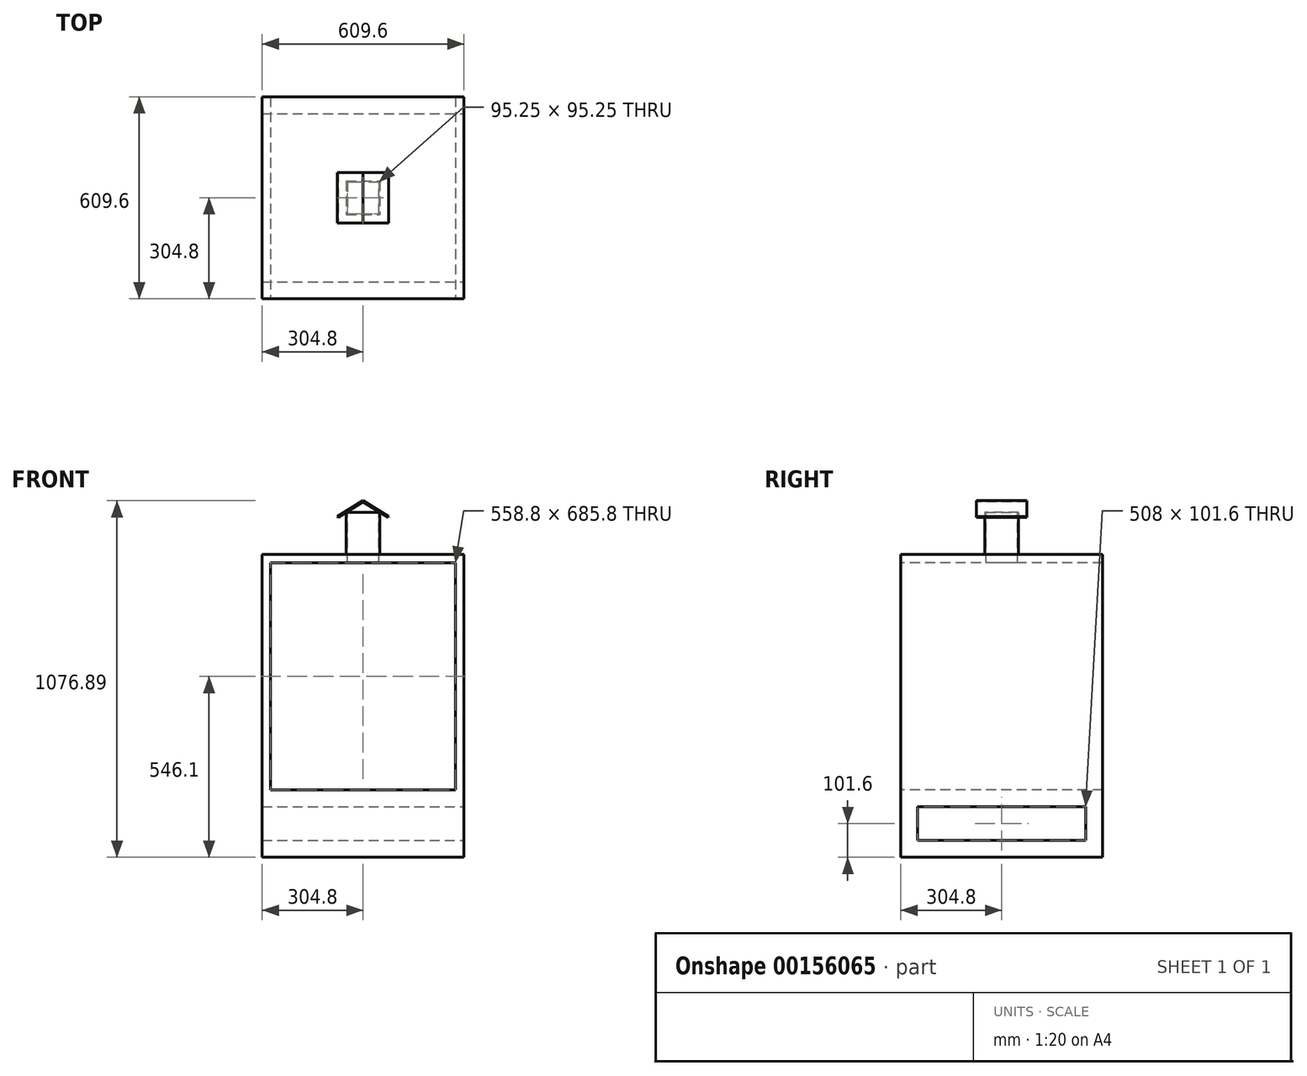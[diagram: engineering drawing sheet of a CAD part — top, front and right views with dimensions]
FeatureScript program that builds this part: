
annotation { "Feature Type Name" : "Feature", "Feature Type Description" : "" }
export const myFeature = defineFeature(function(context is Context, id is Id, definition is map)
    precondition{}
    {
        {
            var Q0;
            Q0=qCreatedBy(makeId("Top.planeOp"),FACE);
            var sketch = newSketch(context, id + "F0", { "sketchPlane" : qUnion([Q0])});
            skLineSegment(sketch, "E0.bottom", {"start": v(0, 0) * mm, "end": v(609.6, 0) * mm});
            skLineSegment(sketch, "E0.top", {"start": v(0, -609.6) * mm, "end": v(609.6, -609.6) * mm});
            skLineSegment(sketch, "E0.left", {"start": v(0, 0) * mm, "end": v(0, -609.6) * mm});
            skLineSegment(sketch, "E0.right", {"start": v(609.6, 0) * mm, "end": v(609.6, -609.6) * mm});
            skSolve(sketch);
        }
        {
            var Q0;
            Q0 = qSketchRegion(id + "F0", true);
            extrude(context, id + "F1", {"entities" : qUnion([Q0]), "depth" : 914.4 * mm});
        }
        {
            var Q0;
            Q0=makeQuery(id+"F1.opExtrude","SWEPT_FACE",FACE,{"disambiguationData":[OSD([sQuery(id+"F0.wireOp",EDGE,"E0.top")])]});
            var sketch = newSketch(context, id + "F2", { "sketchPlane" : qUnion([Q0])});
            skLineSegment(sketch, "E1.bottom", {"start": v(25.4, 889) * mm, "end": v(584.2, 889) * mm});
            skLineSegment(sketch, "E1.top", {"start": v(25.4, 203.2) * mm, "end": v(584.2, 203.2) * mm});
            skLineSegment(sketch, "E1.left", {"start": v(25.4, 889) * mm, "end": v(25.4, 203.2) * mm});
            skLineSegment(sketch, "E1.right", {"start": v(584.2, 889) * mm, "end": v(584.2, 203.2) * mm});
            skSolve(sketch);
        }
        {
            var Q0;
            Q0=makeQuery(id+"F2.imprint","IMPRINT",FACE,{"disambiguationData":[TD([[makeQuery(id+"F2.imprint","IMPRINT",EDGE,{"derivedFrom":sQuery(id+"F2.wireOp",EDGE,"E1.bottom")}),-1.0]])]});
            extrude(context, id + "F3", {"entities" : qUnion([Q0]), "operationType" : NewBodyOperationType.REMOVE, "endBound" : BoundingType.UP_TO_NEXT, "oppositeDirection" : true, "depth" : 25.4 * mm});
        }
        {
            var Q0;
            Q0=makeQuery(id+"F1.opExtrude","SWEPT_FACE",FACE,{"disambiguationData":[OSD([sQuery(id+"F0.wireOp",EDGE,"E0.right")])]});
            var sketch = newSketch(context, id + "F4", { "sketchPlane" : qUnion([Q0])});
            skLineSegment(sketch, "E2.bottom", {"start": v(-558.8, 50.8) * mm, "end": v(-50.8, 50.8) * mm});
            skLineSegment(sketch, "E2.top", {"start": v(-558.8, 152.4) * mm, "end": v(-50.8, 152.4) * mm});
            skLineSegment(sketch, "E2.left", {"start": v(-558.8, 50.8) * mm, "end": v(-558.8, 152.4) * mm});
            skLineSegment(sketch, "E2.right", {"start": v(-50.8, 50.8) * mm, "end": v(-50.8, 152.4) * mm});
            skSolve(sketch);
        }
        {
            var Q0;
            Q0=makeQuery(id+"F4.imprint","IMPRINT",FACE,{"disambiguationData":[TD([[makeQuery(id+"F4.imprint","IMPRINT",EDGE,{"derivedFrom":sQuery(id+"F4.wireOp",EDGE,"E2.bottom")}),1.0]])]});
            extrude(context, id + "F5", {"entities" : qUnion([Q0]), "operationType" : NewBodyOperationType.REMOVE, "endBound" : BoundingType.UP_TO_NEXT, "oppositeDirection" : true, "depth" : 25.4 * mm});
        }
        {
            var Q0;
            Q0=makeQuery(id+"F1.opExtrude","CAP_FACE",FACE,{"disambiguationData":[OSD([sQuery(id+"F0.wireOp",EDGE,"E0.bottom"),sQuery(id+"F0.wireOp",EDGE,"E0.top"),sQuery(id+"F0.wireOp",EDGE,"E0.left"),sQuery(id+"F0.wireOp",EDGE,"E0.right")])],"isStart":false});
            var sketch = newSketch(context, id + "F6", { "sketchPlane" : qUnion([Q0])});
            skLineSegment(sketch, "E3.bottom", {"start": v(254, -254) * mm, "end": v(355.6, -254) * mm});
            skLineSegment(sketch, "E3.top", {"start": v(254, -355.6) * mm, "end": v(355.6, -355.6) * mm});
            skLineSegment(sketch, "E3.left", {"start": v(254, -254) * mm, "end": v(254, -355.6) * mm});
            skLineSegment(sketch, "E3.right", {"start": v(355.6, -254) * mm, "end": v(355.6, -355.6) * mm});
            skSolve(sketch);
        }
        {
            var Q0;
            Q0=makeQuery(id+"F6.imprint","IMPRINT",FACE,{"disambiguationData":[TD([[makeQuery(id+"F6.imprint","IMPRINT",EDGE,{"derivedFrom":sQuery(id+"F6.wireOp",EDGE,"E3.bottom")}),-1.0]])]});
            extrude(context, id + "F7", {"entities" : qUnion([Q0]), "operationType" : NewBodyOperationType.ADD, "depth" : 127 * mm});
        }
        {
            var Q0;
            Q0=makeQuery(id+"F7.opExtrude","CAP_FACE",FACE,{"disambiguationData":[OSD([sQuery(id+"F6.wireOp",EDGE,"E3.bottom"),sQuery(id+"F6.wireOp",EDGE,"E3.top"),sQuery(id+"F6.wireOp",EDGE,"E3.left"),sQuery(id+"F6.wireOp",EDGE,"E3.right")])],"isStart":false});
            var sketch = newSketch(context, id + "F8", { "sketchPlane" : qUnion([Q0])});
            skLineSegment(sketch, "E4.0", {"start": v(352.42, -257.17) * mm, "end": v(257.17, -257.17) * mm});
            skLineSegment(sketch, "E4.1", {"start": v(352.42, -352.42) * mm, "end": v(352.42, -257.17) * mm});
            skLineSegment(sketch, "E4.2", {"start": v(257.17, -352.42) * mm, "end": v(352.42, -352.42) * mm});
            skLineSegment(sketch, "E4.3", {"start": v(257.17, -257.17) * mm, "end": v(257.17, -352.42) * mm});
            skSolve(sketch);
        }
        {
            var Q0;
            Q0=makeQuery(id+"F8.imprint","IMPRINT",FACE,{"disambiguationData":[TD([[makeQuery(id+"F8.imprint","IMPRINT",EDGE,{"derivedFrom":sQuery(id+"F8.wireOp",EDGE,"E4.0")}),1.0]])]});
            extrude(context, id + "F9", {"entities" : qUnion([Q0]), "operationType" : NewBodyOperationType.REMOVE, "endBound" : BoundingType.UP_TO_NEXT, "oppositeDirection" : true, "depth" : 25.4 * mm});
        }
        {
            var Q0;
            Q0=makeQuery(id+"F7.opExtrude","SWEPT_FACE",FACE,{"disambiguationData":[OSD([sQuery(id+"F6.wireOp",EDGE,"E3.top")])]});
            cPlane(context, id + "F10", {"entities" : qUnion([Q0]), "cplaneType" : CPlaneType.OFFSET, "offset" : 25.4 * mm, "width" : 152.4 * mm, "height" : 152.4 * mm});
        }
        {
            var Q0;
            Q0=qCreatedBy(id+"F10.planeOp",FACE);
            var sketch = newSketch(context, id + "F11", { "sketchPlane" : qUnion([Q0])});
            skLineSegment(sketch, "E5.0.0", {"start": v(254, 914.4) * mm, "end": v(355.6, 914.4) * mm});
            skLineSegment(sketch, "E5.0.1", {"start": v(355.6, 914.4) * mm, "end": v(355.6, 1041.4) * mm});
            skLineSegment(sketch, "E5.0.2", {"start": v(355.6, 1041.4) * mm, "end": v(254, 1041.4) * mm});
            skLineSegment(sketch, "E5.0.3", {"start": v(254, 1041.4) * mm, "end": v(254, 914.4) * mm});
            skLineSegment(sketch, "E6", {"start": v(304.8, 1073.15) * mm, "end": v(229.41, 1026.03) * mm});
            skLineSegment(sketch, "E7", {"start": v(229.41, 1026.03) * mm, "end": v(227.73, 1028.73) * mm});
            skLineSegment(sketch, "E8", {"start": v(227.73, 1028.73) * mm, "end": v(304.8, 1076.9) * mm});
            skLineSegment(sketch, "E9.MirrorCS", {"start": v(304.8, 1073.15) * mm, "end": v(380.19, 1026.03) * mm});
            skLineSegment(sketch, "E10.MirrorCS", {"start": v(381.87, 1028.73) * mm, "end": v(304.8, 1076.9) * mm});
            skLineSegment(sketch, "E11.MirrorCS", {"start": v(380.19, 1026.03) * mm, "end": v(381.87, 1028.73) * mm});
            skSolve(sketch);
        }
        {
            var Q0;
            {var subQ0=sQuery(id+"F11.wireOp",EDGE,"E7");Q0=makeQuery(id+"F11.imprint","IMPRINT",FACE,{"disambiguationData":[TD([[makeQuery(id+"F11.imprint","IMPRINT",EDGE,{"derivedFrom":subQ0}),-1.0]])]});}
            extrude(context, id + "F12", {"entities" : qUnion([Q0]), "oppositeDirection" : true, "depth" : 152.4 * mm});
        }
    });
